# Revit family: 13098 Цветочница «Лаванда» Хоббика
name_source: partatom
category: Антураж
revit_build: Autodesk Revit 2018 (Build: 20180423_1000(x64)
units: mm (PartAtom-declared; Revit-internal decimal feet)

## family parameters
Всегда вертикально = Да
Источник визуального образа = Геометрия семейства
На основе рабочей плоскости = Нет
Общий = Нет
При загрузке вырезать с полостями = Нет
Точка расчета площади = Нет

## types (2) — shared parameters
URL = https://hobbyka.ru
Артикул товара = Арт. 13098
Высота = 385 мм
Группа модели = Цветочницы и уличные вазоны для цветов
Длина = 1490 мм
Изготовитель = ООО «Хоббика»
Изображение типоразмера = Цветочница «Лаванда» Арт 13098.jpg
Материал изделия = Дерево
Ширина = 450 мм

## per-type parameters (varying)
| type | Версия Ангарская сосна | Версия Лиственница | Описание | Цвет отделки |
| Версия Ангарская сосна | Да | Нет | Цветочница «Лаванда». Версия Ангорская сосна | Ангарская сосна |
| Версия Лиственница | Нет | Да | Цветочница «Лаванда». Версия Лиственница | Лиственница |
